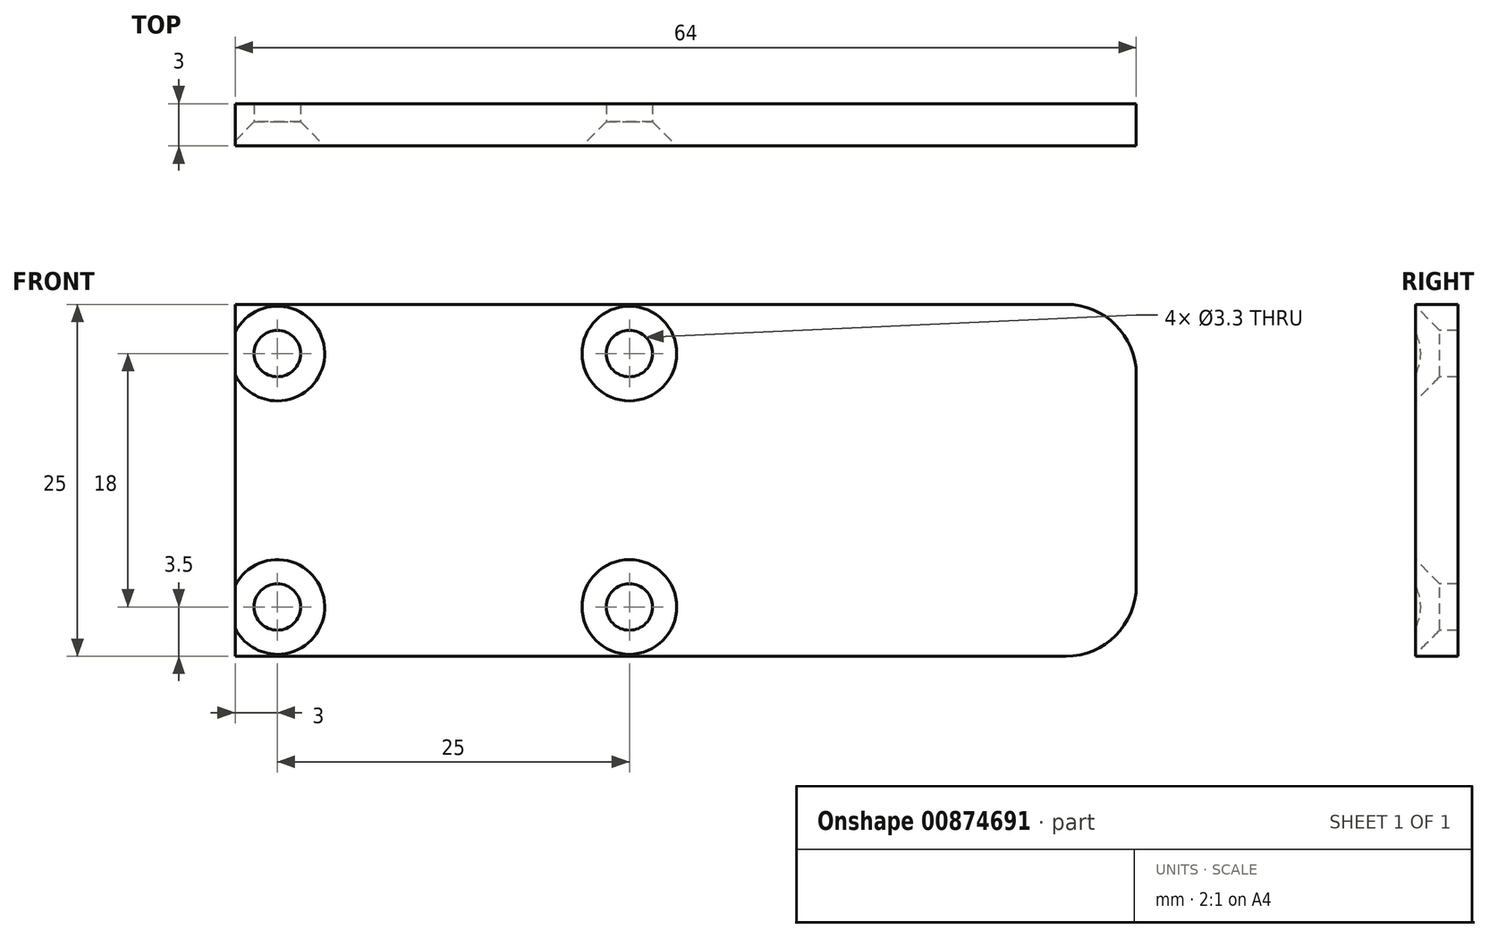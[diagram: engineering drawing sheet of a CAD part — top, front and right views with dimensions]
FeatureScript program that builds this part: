
annotation { "Feature Type Name" : "Feature", "Feature Type Description" : "" }
export const myFeature = defineFeature(function(context is Context, id is Id, definition is map)
    precondition{}
    {
        {
            var Q0;
            Q0=qCreatedBy(makeId("Front.planeOp"),FACE);
            var sketch = newSketch(context, id + "F0", { "sketchPlane" : qUnion([Q0])});
            skLineSegment(sketch, "E0.bottom", {"start": v(0, 0) * mm, "end": v(64, 0) * mm});
            skLineSegment(sketch, "E0.top", {"start": v(0, 25) * mm, "end": v(64, 25) * mm});
            skLineSegment(sketch, "E0.left", {"start": v(0, 0) * mm, "end": v(0, 25) * mm});
            skLineSegment(sketch, "E0.right", {"start": v(64, 0) * mm, "end": v(64, 25) * mm});
            skSolve(sketch);
        }
        {
            var Q0;
            Q0=makeQuery(id+"F0.imprint","IMPRINT",FACE,{"disambiguationData":[TD([[makeQuery(id+"F0.imprint","IMPRINT",EDGE,{"derivedFrom":sQuery(id+"F0.wireOp",EDGE,"E0.bottom")}),1.0]])]});
            extrude(context, id + "F1", {"entities" : qUnion([Q0]), "depth" : 3 * mm, "offsetDistance" : 25 * mm});
        }
        {
            var Q0;
            Q0=makeQuery(id+"F1.opExtrude","CAP_FACE",FACE,{"disambiguationData":[OSD([sQuery(id+"F0.wireOp",EDGE,"E0.bottom"),sQuery(id+"F0.wireOp",EDGE,"E0.top"),sQuery(id+"F0.wireOp",EDGE,"E0.left"),sQuery(id+"F0.wireOp",EDGE,"E0.right")])],"isStart":false});
            var sketch = newSketch(context, id + "F2", { "sketchPlane" : qUnion([Q0])});
            skPoint(sketch, "E1", {"position": v(3, 21.5) * mm});
            skPoint(sketch, "E2", {"position": v(3, 3.5) * mm});
            skPoint(sketch, "E3", {"position": v(28, 3.5) * mm});
            skPoint(sketch, "E4", {"position": v(28, 21.5) * mm});
            skSolve(sketch);
        }
        {
            var Q0;
            Q0=sQuery(id+"F2.wireOp",VERTEX,"E1");
            var Q1;
            Q1=sQuery(id+"F2.wireOp",VERTEX,"E4");
            var Q2;
            Q2=sQuery(id+"F2.wireOp",VERTEX,"E3");
            var Q3;
            Q3=sQuery(id+"F2.wireOp",VERTEX,"E2");
            var Q4;
            Q4=makeQuery(id+"F1.opExtrude","SWEPT_BODY",BODY,{"disambiguationData":[OSD([sQuery(id+"F0.wireOp",EDGE,"E0.bottom"),sQuery(id+"F0.wireOp",EDGE,"E0.top"),sQuery(id+"F0.wireOp",EDGE,"E0.left"),sQuery(id+"F0.wireOp",EDGE,"E0.right")])]});
            hole(context, id + "F3", {"style" : HoleStyle.C_SINK, "endStyle" : HoleEndStyle.THROUGH, "standardTappedOrClearance" : lookupTablePath({ "fit" : "Normal", "standard" : "ISO", "size" : "M3", "type" : "Clearance" }), "standardBlindInLast" : lookupTablePath({ "fit" : "Standard", "standard" : "ISO", "size" : "M3", "type" : "Clearance" }), "holeDiameter" : 3.3 * mm, "cSinkDiameter" : 6.72 * mm, "cSinkAngle" : 90 * degree, "majorDiameter" : 5 * mm, "isTappedThrough" : true, "tappedDepth" : 11.5 * mm, "tapClearance" : 3, "locations" : qUnion([Q0, Q1, Q2, Q3]), "scope" : qUnion([Q4])});
        }
        {
            var Q0;
            Q0=makeQuery(id+"F1.opExtrude","SWEPT_EDGE",EDGE,{"disambiguationData":[OSD([sQuery(id+"F0.wireOp",EDGE,"E0.bottom"),sQuery(id+"F0.wireOp",EDGE,"E0.right")])]});
            var Q1;
            Q1=makeQuery(id+"F1.opExtrude","SWEPT_EDGE",EDGE,{"disambiguationData":[OSD([sQuery(id+"F0.wireOp",EDGE,"E0.top"),sQuery(id+"F0.wireOp",EDGE,"E0.right")])]});
            fillet(context, id + "F4", {"entities" : qUnion([Q0, Q1]), "radius" : 5 * mm, "tangentPropagation" : true, "allowEdgeOverflow" : false});
        }
    });
